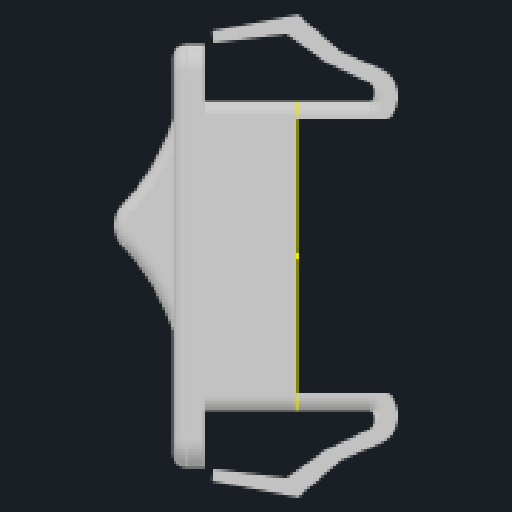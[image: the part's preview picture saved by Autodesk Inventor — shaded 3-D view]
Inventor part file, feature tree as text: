
AUTODESK INVENTOR PART (.ipt)
format: ipt  version: 2023 (Build 270158000, 158)  size: 299,008 bytes
history: native  units: in
note: dims shown in document units (in); Inventor stores cm internally (conversion verified against a paired STEP export)
features: extrude x8, sketch x8, fillet x4, projected_geometry x1
ambient origin geometry x8: Origin, YZ Plane, XZ Plane, XY Plane, X Axis, Y Axis, Z Axis, Center Point
bodies: Solid1 (feature_tree)
feature tree (21):
  extrude  "Extrusion1"  Depth=1.24in
  extrude  "Extrusion2"  Depth=0.36in TaperAngle=0.0deg
  extrude  "Extrusion3"  Depth=0.955in
  fillet  "Fillet1"  Radius=0.0787in
  extrude  "Extrusion4"  Depth=0.3937in
  fillet  "Fillet2"  Radius=0.3937in
  extrude  "Extrusion5"  TaperAngle=0.0deg  [1 undecoded]
  extrude  "Extrusion6"  TaperAngle=0.0deg  [1 undecoded]
  fillet  "Fillet3"  Radius=1.0in
  extrude  "Extrusion7"  TaperAngle=0.0deg  [1 undecoded]
  extrude  "Extrusion8"  Depth=0.0394in
  fillet  "Fillet4"  [1 undecoded]
  sketch  "Sketch1"  dims[d0=0.68in d1=1.24in]
  sketch  "Sketch2"  dims[d2=0.08in d3=0.36in d4=0.0in]
  projected_geometry  "Projected Loop1"
  sketch  "Sketch3"  dims[d5=0.375in d6=0.955in d7=0.0787in]
  sketch  "Sketch4"  dims[d8=0.1181in d9=0.0in d10=0.775in d11=0.3937in d12=0.0in]
  sketch  "Sketch5"  dims[d13=0.0787in d14=0.0in d15=0.0in]
  sketch  "Sketch6"  dims[d16=0.315in d17=0.0in d18=0.0in d19=1.0in d20=0.0in]
  sketch  "Sketch7"  dims[d21=0.0394in d22=0.0in d23=0.0in]
  sketch  "Sketch8"  dims[d24=1.0in d25=0.0in d26=0.0394in]
note: 4 required parameter values undecoded (feature->parameter linkage not recoverable at this tier; creation-order binding heuristic only, values carry confidence <= 0.55)
